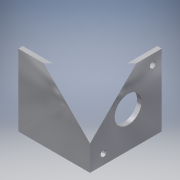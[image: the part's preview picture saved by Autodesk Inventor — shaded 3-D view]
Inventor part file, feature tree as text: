
AUTODESK INVENTOR PART (.ipt)
format: ipt  version: 2016 (Build 200138000, 138)  size: 121,344 bytes
history: native  units: in
note: dims shown in document units (in); Inventor stores cm internally (conversion verified against a paired STEP export)
features: extrude x2, sketch x2
ambient origin geometry x8: Origin, YZ Plane, XZ Plane, XY Plane, X Axis, Y Axis, Z Axis, Center Point
bodies: Solid1 (feature_tree)
feature tree (4):
  extrude  "Extrusion1"  Depth=2.0in
  extrude  "Extrusion2"  Depth=1.875in
  sketch  "Sketch1"  dims[d0=2.0in d1=2.0in]
  sketch  "Sketch3"  dims[d2=0.125in d3=1.875in d4=1.875in d5=2.0in d6=0.0in d12=2.0in d13=1.0in d14=0.9375in d15=0.16in d16=0.16in d17=0.689in d18=0.689in d19=0.75in d20=0.125in d21=0.0in]
